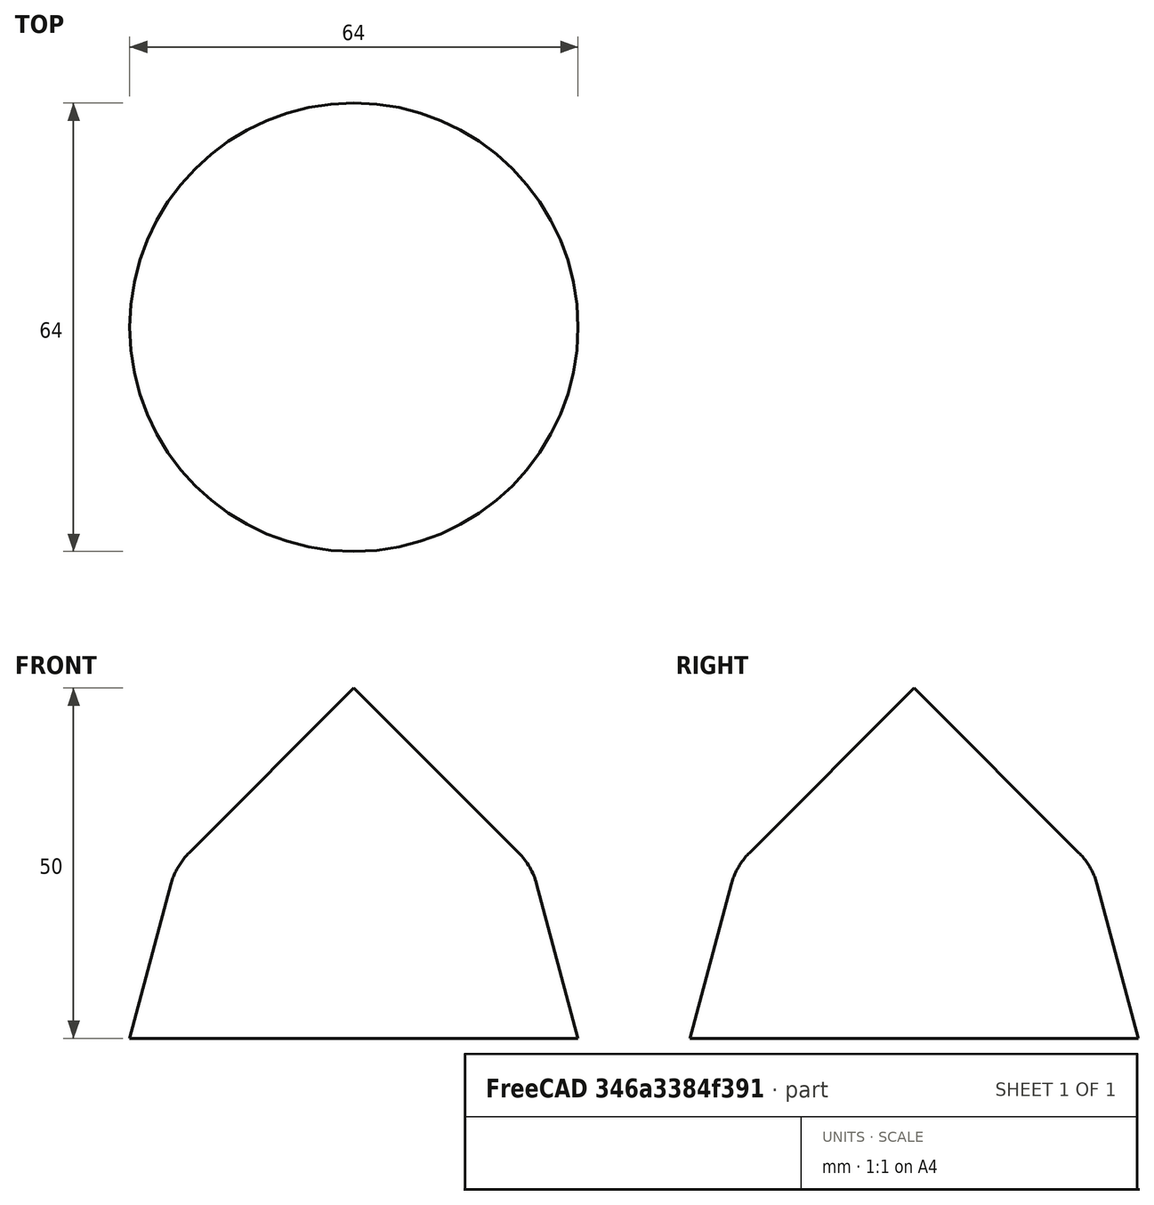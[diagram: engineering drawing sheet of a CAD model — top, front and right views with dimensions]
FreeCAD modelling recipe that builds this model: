
FCSTD DOCUMENT  (FreeCAD 0.20R29177 (Git))
Label: spire-jurt
License: Creative Commons Attribution-ShareAlike
LicenseURL: http://creativecommons.org/licenses/by-sa/4.0/
objects: Sketcher::SketchObject×1, PartDesign::Revolution×1, PartDesign::Body×1
note: 4 computed .brp shape members not serialized (recipe doc carries the construction recipe); baked Part::Feature solids carry a one-line shape summary decoded from their .brp

FEATURE [Sketcher::SketchObject] Sketch
  FullyConstrained = true
  MapMode = 5
  Placement = pos=(0,0,0) rot=(1,0,0;1.5708rad)
  Support = -> [XZ_Plane]
  sketch-geometry (5):
    g0: LineSegment StartX=0 StartY=50 StartZ=0 EndX=23.5169 EndY=26.4831 EndZ=0
    g1: LineSegment StartX=26.105 StartY=22.0003 StartZ=0 EndX=32 EndY=0 EndZ=0
    g2: LineSegment StartX=32 StartY=0 StartZ=0 EndX=0 EndY=0 EndZ=0
    g3: LineSegment StartX=0 StartY=0 StartZ=0 EndX=0 EndY=50 EndZ=0
    g4: ArcOfCircle CenterX=16.4458 CenterY=19.4121 CenterZ=0 NormalX=0 NormalY=0 NormalZ=1 AngleXU=0 Radius=10 StartAngle=0.261799 EndAngle=0.785398
  constraints (13):
    c: PointOnObject(g0,g-2)
    c: Coincident(g1,g2)
    c: Coincident(g2,g-1)
    c: Horizontal(g2)
    c: Coincident(g2,g3)
    c: Coincident(g3,g0)
    c: Tangent(g0,g4) = 1.5708
    c: Tangent(g1,g4) = 1.5708
    c: Angle(g-2,g0) = 0.785398
    c: Angle(g-2,g1) = 0.261799
    c: Distance(g2) = 32
    c: Distance(g3) = 50
    c: Diameter(g4) = 20
FEATURE [PartDesign::Revolution] Revolution
  Angle = 360
  Axis = (0,2e-16,1)
  Base = (0,0,0)
  Placement = pos=(0,0,0) rot=(1,0,0;1.5708rad)
  Profile = -> Sketch
  ReferenceAxis = -> Sketch [V_Axis]
  Reversed = true
FEATURE [PartDesign::Body] Body
  Group = -> [Sketch,Revolution]
  Origin = -> Origin
  Tip = -> Revolution
